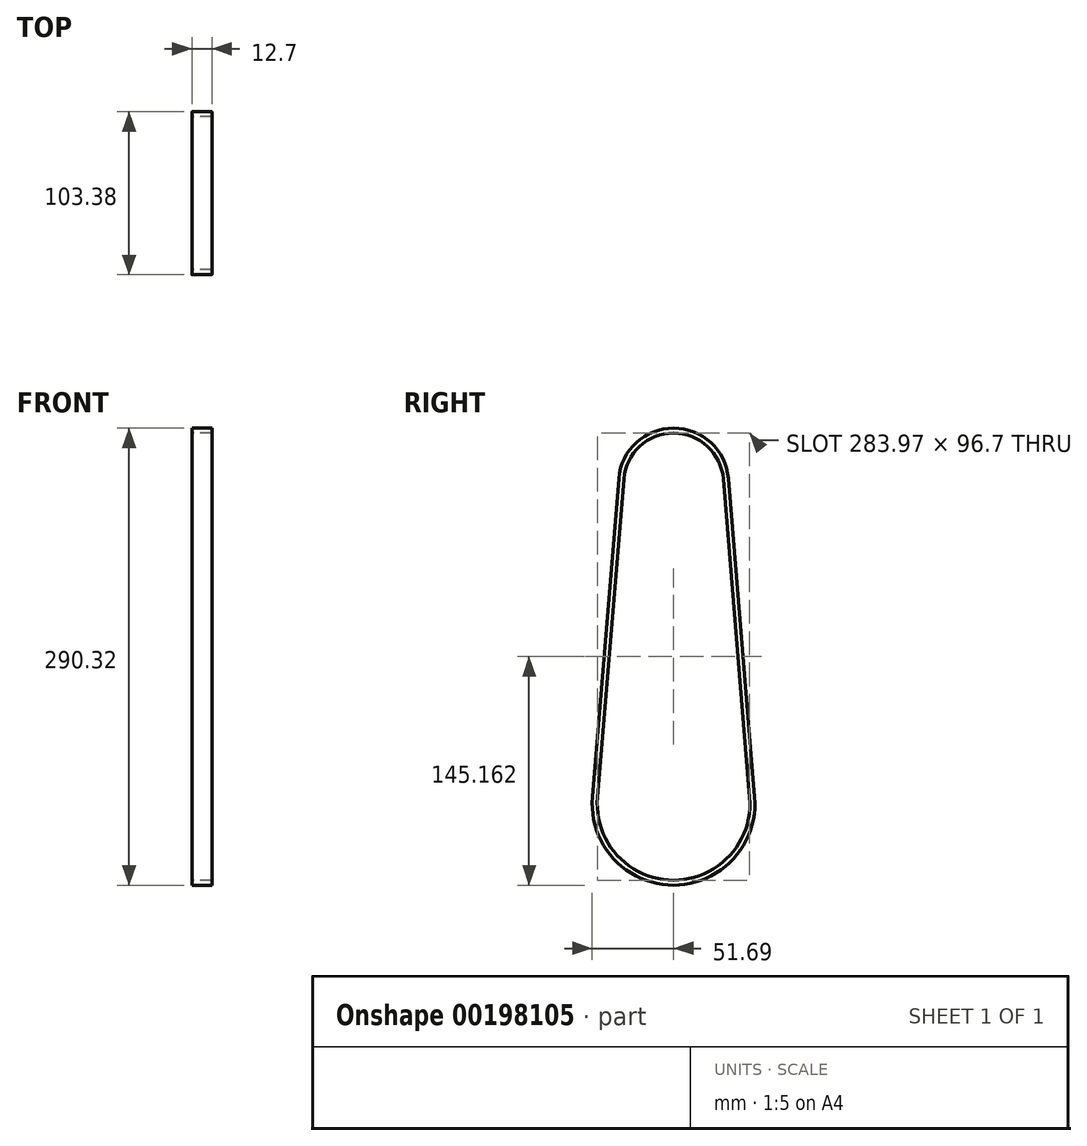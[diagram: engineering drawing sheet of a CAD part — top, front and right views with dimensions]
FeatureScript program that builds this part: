
annotation { "Feature Type Name" : "Feature", "Feature Type Description" : "" }
export const myFeature = defineFeature(function(context is Context, id is Id, definition is map)
    precondition{}
    {
        {
            var Q0;
            Q0=qCreatedBy(makeId("Right.planeOp"),FACE);
            var sketch = newSketch(context, id + "F0", { "sketchPlane" : qUnion([Q0])});
            skArc(sketch, "E0", {"start": v(-48.35, 4) * mm, "mid": v(0, -48.51) * mm, "end": v(48.35, 4) * mm});
            skLineSegment(sketch, "E1", {"start": v(0, 0) * mm, "end": v(0, 203.7) * mm, "construction": true});
            skArc(sketch, "E2", {"start": v(31.64, 206.32) * mm, "mid": v(0, 235.46) * mm, "end": v(-31.64, 206.32) * mm});
            skArc(sketch, "E3.0", {"start": v(-51.51, 4.25) * mm, "mid": v(0, -51.69) * mm, "end": v(51.51, 4.25) * mm});
            skArc(sketch, "E4.0", {"start": v(34.8, 206.58) * mm, "mid": v(0, 238.63) * mm, "end": v(-34.8, 206.58) * mm});
            skLineSegment(sketch, "E5", {"start": v(-31.64, 206.32) * mm, "end": v(-48.35, 4) * mm});
            skLineSegment(sketch, "E6", {"start": v(-34.8, 206.58) * mm, "end": v(-51.86, 0) * mm});
            skLineSegment(sketch, "E7.MirrorCS", {"start": v(34.8, 206.58) * mm, "end": v(51.86, 0) * mm});
            skLineSegment(sketch, "E8.MirrorCS", {"start": v(31.64, 206.32) * mm, "end": v(48.35, 4) * mm});
            skSolve(sketch);
        }
        {
            var Q0;
            Q0 = qSketchRegion(id + "F0", true);
            extrude(context, id + "F1", {"entities" : qUnion([Q0]), "endBound" : BoundingType.SYMMETRIC, "depth" : 12.7 * mm});
        }
    });
